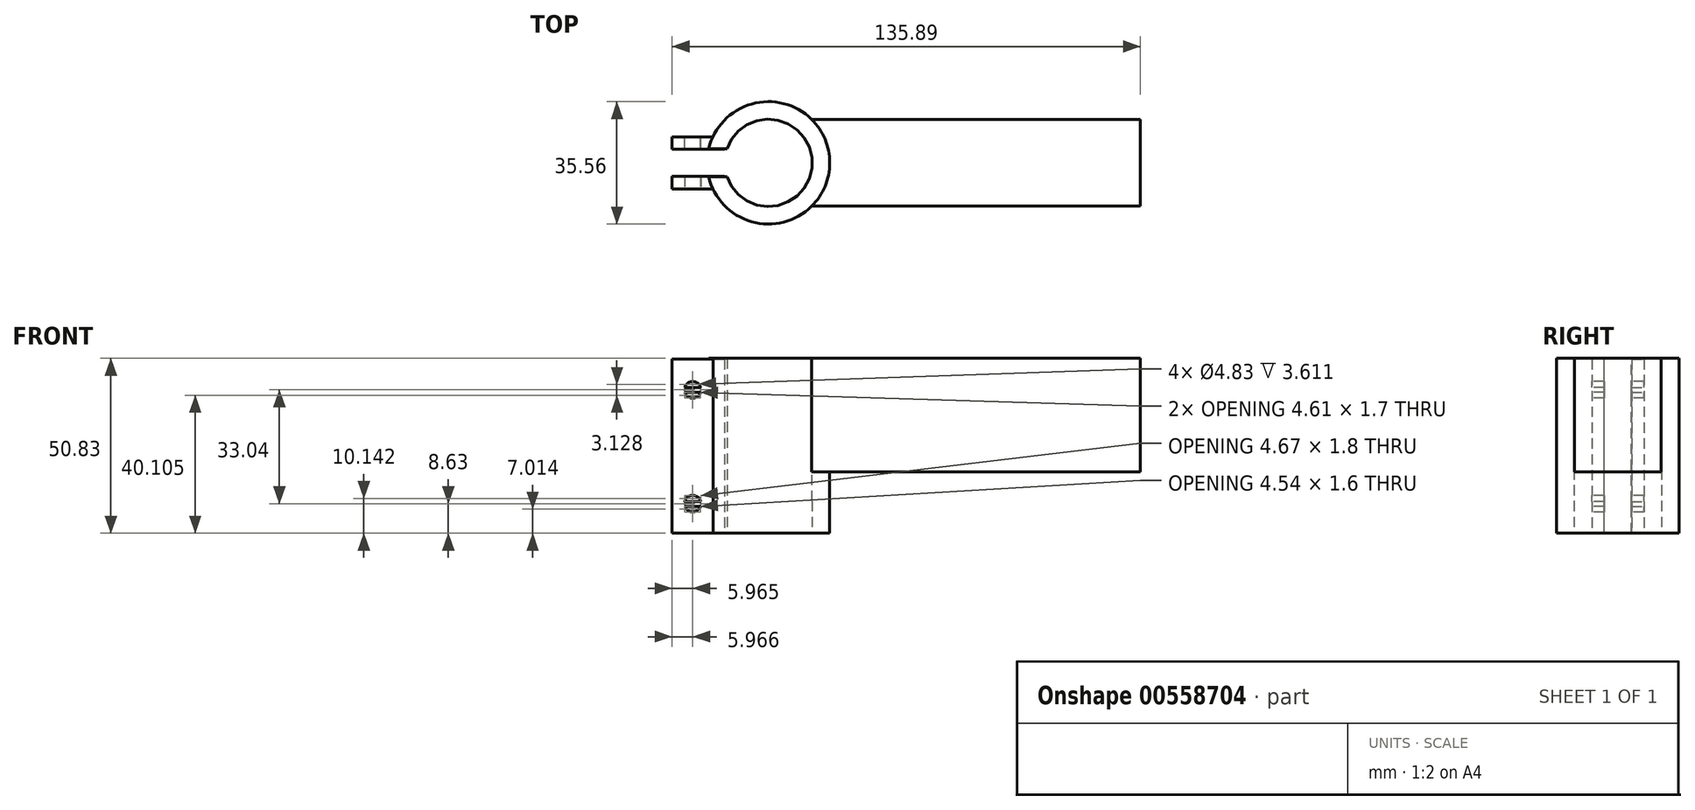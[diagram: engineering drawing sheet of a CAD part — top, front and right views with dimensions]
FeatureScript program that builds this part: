
annotation { "Feature Type Name" : "Feature", "Feature Type Description" : "" }
export const myFeature = defineFeature(function(context is Context, id is Id, definition is map)
    precondition{}
    {
        {
            var Q0;
            Q0=qCreatedBy(makeId("Top.planeOp"),FACE);
            var sketch = newSketch(context, id + "F0", { "sketchPlane" : qUnion([Q0])});
            skCircle(sketch, "E0", {"center": v(0, 0) * mm, "radius": 17.78 * mm});
            skCircle(sketch, "E1", {"center": v(0, 0) * mm, "radius": 12.7 * mm});
            skSolve(sketch);
        }
        {
            var Q0;
            Q0=makeQuery(id+"F0.imprint","IMPRINT",FACE,{"disambiguationData":[TD([[makeQuery(id+"F0.imprint","IMPRINT",EDGE,{"derivedFrom":sQuery(id+"F0.wireOp",EDGE,"E0")}),1.0]])]});
            extrude(context, id + "F1", {"entities" : qUnion([Q0]), "depth" : 50.8 * mm, "offsetDistance" : 25.4 * mm});
        }
        {
            var Q0;
            Q0=qCreatedBy(makeId("Right.planeOp"),FACE);
            var sketch = newSketch(context, id + "F2", { "sketchPlane" : qUnion([Q0])});
            skLineSegment(sketch, "E2.bottom", {"start": v(4.04, -22.05) * mm, "end": v(-4.04, -22.05) * mm});
            skLineSegment(sketch, "E2.top", {"start": v(4.04, 74.5) * mm, "end": v(-4.04, 74.5) * mm});
            skLineSegment(sketch, "E2.left", {"start": v(4.04, -22.05) * mm, "end": v(4.04, 74.5) * mm});
            skLineSegment(sketch, "E2.right", {"start": v(-4.04, -22.05) * mm, "end": v(-4.04, 74.5) * mm});
            skPoint(sketch, "E2.middle", {"position": v(0, 26.22) * mm});
            skSolve(sketch);
        }
        {
            var Q0;
            Q0 = qSketchRegion(id + "F2", true);
            extrude(context, id + "F3", {"entities" : qUnion([Q0]), "operationType" : NewBodyOperationType.REMOVE, "oppositeDirection" : true, "depth" : 25.4 * mm, "offsetDistance" : 25.4 * mm});
        }
        {
            var Q0;
            Q0=qCreatedBy(makeId("Right.planeOp"),FACE);
            var sketch = newSketch(context, id + "F4", { "sketchPlane" : qUnion([Q0])});
            skLineSegment(sketch, "E3.bottom", {"start": v(-3.96, 0) * mm, "end": v(-7.57, 0) * mm});
            skLineSegment(sketch, "E3.top", {"start": v(-3.96, 50.58) * mm, "end": v(-7.57, 50.58) * mm});
            skLineSegment(sketch, "E3.left", {"start": v(-3.96, 0) * mm, "end": v(-3.96, 50.58) * mm});
            skLineSegment(sketch, "E3.right", {"start": v(-7.57, 0) * mm, "end": v(-7.57, 50.58) * mm});
            skSolve(sketch);
        }
        {
            var Q0;
            Q0 = qSketchRegion(id + "F4", true);
            extrude(context, id + "F5", {"entities" : qUnion([Q0]), "operationType" : NewBodyOperationType.ADD, "oppositeDirection" : true, "depth" : 27.94 * mm, "offsetDistance" : 25.4 * mm});
        }
        {
            var Q0;
            Q0=makeQuery(id+"F5.opExtrude","CAP_FACE",FACE,{"disambiguationData":[OSD([sQuery(id+"F4.wireOp",EDGE,"E3.bottom"),sQuery(id+"F4.wireOp",EDGE,"E3.top"),sQuery(id+"F4.wireOp",EDGE,"E3.left"),sQuery(id+"F4.wireOp",EDGE,"E3.right")])],"isStart":true});
            extrude(context, id + "F6", {"entities" : qUnion([Q0]), "operationType" : NewBodyOperationType.REMOVE, "oppositeDirection" : true, "depth" : 12.7 * mm, "offsetDistance" : 25.4 * mm});
        }
        {
            var Q0;
            Q0=makeQuery(id+"F1.opExtrude","SWEPT_BODY",BODY,{"disambiguationData":[OSD([sQuery(id+"F0.wireOp",EDGE,"E0"),sQuery(id+"F0.wireOp",EDGE,"E1")])]});
            var Q1;
            Q1=qCreatedBy(makeId("Front.planeOp"),FACE);
            mirror(context, id + "F7", {"operationType" : NewBodyOperationType.ADD, "entities" : qUnion([Q0]), "mirrorPlane" : qUnion([Q1])});
        }
        {
            var Q0;
            Q0=qCreatedBy(makeId("Right.planeOp"),FACE);
            var sketch = newSketch(context, id + "F8", { "sketchPlane" : qUnion([Q0])});
            skLineSegment(sketch, "E4.bottom", {"start": v(12.61, 9.37) * mm, "end": v(-12.61, 9.37) * mm});
            skLineSegment(sketch, "E4.top", {"start": v(12.61, 42.43) * mm, "end": v(-12.61, 42.43) * mm});
            skLineSegment(sketch, "E4.left", {"start": v(12.61, 9.37) * mm, "end": v(12.61, 42.43) * mm});
            skLineSegment(sketch, "E4.right", {"start": v(-12.61, 9.37) * mm, "end": v(-12.61, 42.43) * mm});
            skPoint(sketch, "E4.middle", {"position": v(0, 25.9) * mm});
            skSolve(sketch);
        }
        {
            var Q0;
            Q0 = qSketchRegion(id + "F8", true);
            extrude(context, id + "F9", {"entities" : qUnion([Q0]), "operationType" : NewBodyOperationType.ADD, "depth" : 107.95 * mm, "offsetDistance" : 25.4 * mm});
        }
        {
            var Q0;
            Q0=makeQuery(id+"F1.opExtrude","CAP_FACE",FACE,{"disambiguationData":[OSD([sQuery(id+"F0.wireOp",EDGE,"E0"),sQuery(id+"F0.wireOp",EDGE,"E1")])],"isStart":false});
            var sketch = newSketch(context, id + "F10", { "sketchPlane" : qUnion([Q0])});
            skCircle(sketch, "E5", {"center": v(0, 0) * mm, "radius": 12.7 * mm});
            skSolve(sketch);
        }
        {
            var Q0;
            Q0 = qSketchRegion(id + "F10", true);
            extrude(context, id + "F11", {"entities" : qUnion([Q0]), "operationType" : NewBodyOperationType.REMOVE, "oppositeDirection" : true, "depth" : 50.8 * mm, "offsetDistance" : 25.4 * mm});
        }
        {
            var Q0;
            {var subQ2=sQuery(id+"F8.wireOp",EDGE,"E4.bottom");Q0=makeQuery(id+"F9.boolean.opBoolean","SPLIT",FACE,{"disambiguationData":[TD([makeQuery(id+"F1.opExtrude","SWEPT_FACE",FACE,{"disambiguationData":[OSD([sQuery(id+"F0.wireOp",EDGE,"E0")])]})])],"derivedFrom":makeQuery(id+"F9.opExtrude","SWEPT_FACE",FACE,{"disambiguationData":[OSD([subQ2])]})});}
            extrude(context, id + "F12", {"entities" : qUnion([Q0]), "operationType" : NewBodyOperationType.ADD, "depth" : 9.37 * mm, "offsetDistance" : 25.4 * mm});
        }
        {
            var Q0;
            {var subQ2=sQuery(id+"F8.wireOp",EDGE,"E4.top");Q0=makeQuery(id+"F9.boolean.opBoolean","SPLIT",FACE,{"disambiguationData":[TD([makeQuery(id+"F1.opExtrude","SWEPT_FACE",FACE,{"disambiguationData":[OSD([sQuery(id+"F0.wireOp",EDGE,"E0")])]})])],"derivedFrom":makeQuery(id+"F9.opExtrude","SWEPT_FACE",FACE,{"disambiguationData":[OSD([subQ2])]})});}
            extrude(context, id + "F13", {"entities" : qUnion([Q0]), "operationType" : NewBodyOperationType.REMOVE, "oppositeDirection" : true, "depth" : 9.37 * mm, "offsetDistance" : 25.4 * mm});
        }
        {
            var Q0;
            {var subQ0=sQuery(id+"F4.wireOp",EDGE,"E3.right");var subQ3=sQuery(id+"F0.wireOp",EDGE,"E0");Q0=makeQuery(id+"F5.boolean.opBoolean","SPLIT",FACE,{"disambiguationData":[TD([makeQuery(id+"F1.opExtrude","SWEPT_FACE",FACE,{"disambiguationData":[OSD([subQ3])]})])],"derivedFrom":makeQuery(id+"F5.opExtrude","SWEPT_FACE",FACE,{"disambiguationData":[OSD([subQ0])]})});}
            var sketch = newSketch(context, id + "F14", { "sketchPlane" : qUnion([Q0])});
            skCircle(sketch, "E6", {"center": v(-21.97, 8.63) * mm, "radius": 2.41 * mm});
            skCircle(sketch, "E7", {"center": v(-21.97, 41.67) * mm, "radius": 2.41 * mm});
            skSolve(sketch);
        }
        {
            var Q0;
            Q0 = qSketchRegion(id + "F14", true);
            extrude(context, id + "F15", {"entities" : qUnion([Q0]), "operationType" : NewBodyOperationType.REMOVE, "oppositeDirection" : true, "depth" : 25.4 * mm, "offsetDistance" : 25.4 * mm});
        }
        {
            var Q0;
            {var subQ0=sQuery(id+"F8.wireOp",EDGE,"E4.right");var subQ1=sQuery(id+"F8.wireOp",EDGE,"E4.bottom");Q0=makeQuery(id+"F12.boolean.opBoolean","MERGE",FACE,{"derivedFrom":[makeQuery(id+"F9.boolean.opBoolean","SPLIT",FACE,{"disambiguationData":[TD([makeQuery(id+"F1.opExtrude","SWEPT_FACE",FACE,{"disambiguationData":[OSD([sQuery(id+"F0.wireOp",EDGE,"E0")])]})])],"derivedFrom":makeQuery(id+"F9.opExtrude","SWEPT_FACE",FACE,{"disambiguationData":[OSD([subQ0])]})}),makeQuery(id+"F12.opExtrude","SWEPT_FACE",FACE,{"disambiguationData":[OSD([subQ1,subQ0])]})]});}
            var sketch = newSketch(context, id + "F16", { "sketchPlane" : qUnion([Q0])});
            skLineSegment(sketch, "E8.bottom", {"start": v(102.87, 33.05) * mm, "end": v(107.95, 33.05) * mm});
            skLineSegment(sketch, "E8.top", {"start": v(102.87, 0) * mm, "end": v(107.95, 0) * mm});
            skLineSegment(sketch, "E8.left", {"start": v(102.87, 33.05) * mm, "end": v(102.87, 0) * mm});
            skLineSegment(sketch, "E8.right", {"start": v(107.95, 33.05) * mm, "end": v(107.95, 0) * mm});
            skSolve(sketch);
        }
        {
            var Q0;
            Q0 = qSketchRegion(id + "F16", true);
            extrude(context, id + "F17", {"entities" : qUnion([Q0]), "operationType" : NewBodyOperationType.ADD, "depth" : 6.35 * mm, "offsetDistance" : 25.4 * mm});
        }
        {
            var Q0;
            Q0=makeQuery(id+"F1.opExtrude","SWEPT_BODY",BODY,{"disambiguationData":[OSD([sQuery(id+"F0.wireOp",EDGE,"E0"),sQuery(id+"F0.wireOp",EDGE,"E1")])]});
            var Q1;
            Q1=qCreatedBy(makeId("Front.planeOp"),FACE);
            mirror(context, id + "F18", {"operationType" : NewBodyOperationType.ADD, "entities" : qUnion([Q0]), "mirrorPlane" : qUnion([Q1])});
        }
        {
            var Q0;
            Q0=makeQuery(id+"F17.opExtrude","CAP_FACE",FACE,{"disambiguationData":[OSD([sQuery(id+"F16.wireOp",EDGE,"E8.bottom"),sQuery(id+"F16.wireOp",EDGE,"E8.top"),sQuery(id+"F16.wireOp",EDGE,"E8.left"),sQuery(id+"F16.wireOp",EDGE,"E8.right")])],"isStart":false});
            extrude(context, id + "F19", {"entities" : qUnion([Q0]), "operationType" : NewBodyOperationType.REMOVE, "oppositeDirection" : true, "depth" : 2.54 * mm, "offsetDistance" : 25.4 * mm});
        }
        {
            var Q0;
            Q0=makeQuery(id+"F18.opPattern","COPY",FACE,{"derivedFrom":makeQuery(id+"F17.opExtrude","CAP_FACE",FACE,{"disambiguationData":[OSD([sQuery(id+"F16.wireOp",EDGE,"E8.bottom"),sQuery(id+"F16.wireOp",EDGE,"E8.top"),sQuery(id+"F16.wireOp",EDGE,"E8.left"),sQuery(id+"F16.wireOp",EDGE,"E8.right")])],"isStart":false}),"instanceName":"1"});
            extrude(context, id + "F20", {"entities" : qUnion([Q0]), "operationType" : NewBodyOperationType.REMOVE, "oppositeDirection" : true, "depth" : 2.54 * mm, "offsetDistance" : 25.4 * mm});
        }
        {
            var Q0;
            {var subQ0=makeQuery(id+"F17.boolean.opBoolean","MERGE",FACE,{"derivedFrom":[makeQuery(id+"F13.boolean.opBoolean","COPY",FACE,{"derivedFrom":makeQuery(id+"F13.opExtrude","CAP_FACE",FACE,{"disambiguationData":[OSD([sQuery(id+"F8.wireOp",EDGE,"E4.top")])],"isStart":false})}),makeQuery(id+"F17.opExtrude","SWEPT_FACE",FACE,{"disambiguationData":[OSD([sQuery(id+"F16.wireOp",EDGE,"E8.bottom")])]})]});Q0=makeQuery(id+"F18.boolean.opBoolean","MERGE",FACE,{"derivedFrom":[subQ0,makeQuery(id+"F18.opPattern","COPY",FACE,{"derivedFrom":subQ0,"instanceName":"1"})]});}
            extrude(context, id + "F21", {"entities" : qUnion([Q0]), "operationType" : NewBodyOperationType.ADD, "depth" : 7.62 * mm, "offsetDistance" : 25.4 * mm});
        }
        {
            var Q0;
            {var subQ0=makeQuery(id+"F17.boolean.opBoolean","MERGE",FACE,{"derivedFrom":[makeQuery(id+"F12.opExtrude","CAP_FACE",FACE,{"disambiguationData":[OSD([sQuery(id+"F8.wireOp",EDGE,"E4.bottom")])],"isStart":false}),makeQuery(id+"F17.opExtrude","SWEPT_FACE",FACE,{"disambiguationData":[OSD([sQuery(id+"F16.wireOp",EDGE,"E8.top")])]})]});Q0=makeQuery(id+"F18.boolean.opBoolean","MERGE",FACE,{"derivedFrom":[subQ0,makeQuery(id+"F18.opPattern","COPY",FACE,{"derivedFrom":subQ0,"instanceName":"1"})]});}
            extrude(context, id + "F22", {"entities" : qUnion([Q0]), "operationType" : NewBodyOperationType.REMOVE, "oppositeDirection" : true, "depth" : 7.62 * mm, "offsetDistance" : 25.4 * mm});
        }
        {
            var Q0;
            {var subQ0=sQuery(id+"F4.wireOp",EDGE,"E3.right");var subQ3=sQuery(id+"F0.wireOp",EDGE,"E0");Q0=makeQuery(id+"F5.boolean.opBoolean","SPLIT",FACE,{"disambiguationData":[TD([makeQuery(id+"F1.opExtrude","SWEPT_FACE",FACE,{"disambiguationData":[OSD([subQ3])]})])],"derivedFrom":makeQuery(id+"F5.opExtrude","SWEPT_FACE",FACE,{"disambiguationData":[OSD([subQ0])]})});}
            var sketch = newSketch(context, id + "F23", { "sketchPlane" : qUnion([Q0])});
            skLineSegment(sketch, "E9.bottom", {"start": v(-18.54, 40.95) * mm, "end": v(-25.4, 40.95) * mm});
            skLineSegment(sketch, "E9.top", {"start": v(-18.54, 42.38) * mm, "end": v(-25.4, 42.38) * mm});
            skLineSegment(sketch, "E9.left", {"start": v(-18.54, 40.95) * mm, "end": v(-18.54, 42.38) * mm});
            skLineSegment(sketch, "E9.right", {"start": v(-25.4, 40.95) * mm, "end": v(-25.4, 42.38) * mm});
            skPoint(sketch, "E9.middle", {"position": v(-21.97, 41.67) * mm});
            skLineSegment(sketch, "E10.bottom", {"start": v(-18.56, 7.81) * mm, "end": v(-25.43, 7.81) * mm});
            skLineSegment(sketch, "E10.top", {"start": v(-18.56, 9.24) * mm, "end": v(-25.43, 9.24) * mm});
            skLineSegment(sketch, "E10.left", {"start": v(-18.56, 7.81) * mm, "end": v(-18.56, 9.24) * mm});
            skLineSegment(sketch, "E10.right", {"start": v(-25.43, 7.81) * mm, "end": v(-25.43, 9.24) * mm});
            skSolve(sketch);
        }
        {
            var Q0;
            Q0 = qSketchRegion(id + "F23", true);
            extrude(context, id + "F24", {"entities" : qUnion([Q0]), "operationType" : NewBodyOperationType.ADD, "oppositeDirection" : true, "depth" : 3.56 * mm, "offsetDistance" : 25.4 * mm});
        }
        {
            var Q0;
            Q0=makeQuery(id+"F1.opExtrude","SWEPT_BODY",BODY,{"disambiguationData":[OSD([sQuery(id+"F0.wireOp",EDGE,"E0"),sQuery(id+"F0.wireOp",EDGE,"E1")])]});
            var Q1;
            Q1=qCreatedBy(makeId("Front.planeOp"),FACE);
            mirror(context, id + "F25", {"operationType" : NewBodyOperationType.ADD, "entities" : qUnion([Q0]), "mirrorPlane" : qUnion([Q1])});
        }
        {
            var Q0;
            {var subQ0=sQuery(id+"F16.wireOp",EDGE,"E8.bottom");Q0=makeQuery(id+"F21.boolean.opBoolean","MERGE",FACE,{"derivedFrom":[makeQuery(id+"F19.boolean.opBoolean","COPY",FACE,{"derivedFrom":makeQuery(id+"F19.opExtrude","CAP_FACE",FACE,{"disambiguationData":[OSD([subQ0,sQuery(id+"F16.wireOp",EDGE,"E8.top"),sQuery(id+"F16.wireOp",EDGE,"E8.left"),sQuery(id+"F16.wireOp",EDGE,"E8.right")])],"isStart":false})}),makeQuery(id+"F21.opExtrude","SWEPT_FACE",FACE,{"disambiguationData":[OSD([subQ0]),TDD([makeQuery(id+"F19.boolean.opBoolean","COPY",EDGE,{"derivedFrom":makeQuery(id+"F19.opExtrude","CAP_EDGE",EDGE,{"disambiguationData":[OSD([subQ0])],"isStart":false})})])]})]});}
            extrude(context, id + "F26", {"entities" : qUnion([Q0]), "operationType" : NewBodyOperationType.REMOVE, "oppositeDirection" : true, "depth" : 2.54 * mm, "offsetDistance" : 25.4 * mm});
        }
        {
            var Q0;
            {var subQ0=sQuery(id+"F16.wireOp",EDGE,"E8.bottom");Q0=makeQuery(id+"F21.boolean.opBoolean","MERGE",FACE,{"derivedFrom":[makeQuery(id+"F20.boolean.opBoolean","COPY",FACE,{"derivedFrom":makeQuery(id+"F20.opExtrude","CAP_FACE",FACE,{"disambiguationData":[OSD([subQ0,sQuery(id+"F16.wireOp",EDGE,"E8.top"),sQuery(id+"F16.wireOp",EDGE,"E8.left"),sQuery(id+"F16.wireOp",EDGE,"E8.right")])],"isStart":false})}),makeQuery(id+"F21.opExtrude","SWEPT_FACE",FACE,{"disambiguationData":[OSD([subQ0]),TDD([makeQuery(id+"F20.boolean.opBoolean","COPY",EDGE,{"derivedFrom":makeQuery(id+"F20.opExtrude","CAP_EDGE",EDGE,{"disambiguationData":[OSD([subQ0])],"isStart":false})})])]})]});}
            extrude(context, id + "F27", {"entities" : qUnion([Q0]), "operationType" : NewBodyOperationType.REMOVE, "oppositeDirection" : true, "depth" : 2.54 * mm, "offsetDistance" : 25.4 * mm});
        }
        {
            var Q0;
            Q0=makeQuery(id+"F26.boolean.opBoolean","COPY",FACE,{"derivedFrom":makeQuery(id+"F26.opExtrude","CAP_FACE",FACE,{"disambiguationData":[OSD([sQuery(id+"F16.wireOp",EDGE,"E8.bottom"),sQuery(id+"F16.wireOp",EDGE,"E8.top"),sQuery(id+"F16.wireOp",EDGE,"E8.left"),sQuery(id+"F16.wireOp",EDGE,"E8.right")])],"isStart":false})});
            extrude(context, id + "F28", {"entities" : qUnion([Q0]), "operationType" : NewBodyOperationType.REMOVE, "oppositeDirection" : true, "depth" : 1.27 * mm, "offsetDistance" : 25.4 * mm});
        }
        {
            var Q0;
            Q0=makeQuery(id+"F27.boolean.opBoolean","COPY",FACE,{"derivedFrom":makeQuery(id+"F27.opExtrude","CAP_FACE",FACE,{"disambiguationData":[OSD([sQuery(id+"F16.wireOp",EDGE,"E8.bottom"),sQuery(id+"F16.wireOp",EDGE,"E8.top"),sQuery(id+"F16.wireOp",EDGE,"E8.left"),sQuery(id+"F16.wireOp",EDGE,"E8.right")])],"isStart":false})});
            extrude(context, id + "F29", {"entities" : qUnion([Q0]), "operationType" : NewBodyOperationType.REMOVE, "oppositeDirection" : true, "depth" : 1.27 * mm, "offsetDistance" : 25.4 * mm});
        }
        {
            var Q0;
            Q0=makeQuery(id+"F21.opExtrude","CAP_FACE",FACE,{"disambiguationData":[OSD([sQuery(id+"F8.wireOp",EDGE,"E4.top"),sQuery(id+"F16.wireOp",EDGE,"E8.bottom")])],"isStart":false});
            extrude(context, id + "F30", {"entities" : qUnion([Q0]), "operationType" : NewBodyOperationType.ADD, "depth" : 10.16 * mm, "offsetDistance" : 25.4 * mm});
        }
        {
            var Q0;
            Q0=makeQuery(id+"F22.boolean.opBoolean","COPY",FACE,{"derivedFrom":makeQuery(id+"F22.opExtrude","CAP_FACE",FACE,{"disambiguationData":[OSD([sQuery(id+"F8.wireOp",EDGE,"E4.bottom"),sQuery(id+"F16.wireOp",EDGE,"E8.top")])],"isStart":false})});
            extrude(context, id + "F31", {"entities" : qUnion([Q0]), "operationType" : NewBodyOperationType.REMOVE, "oppositeDirection" : true, "depth" : 10.16 * mm, "offsetDistance" : 25.4 * mm});
        }
    });
